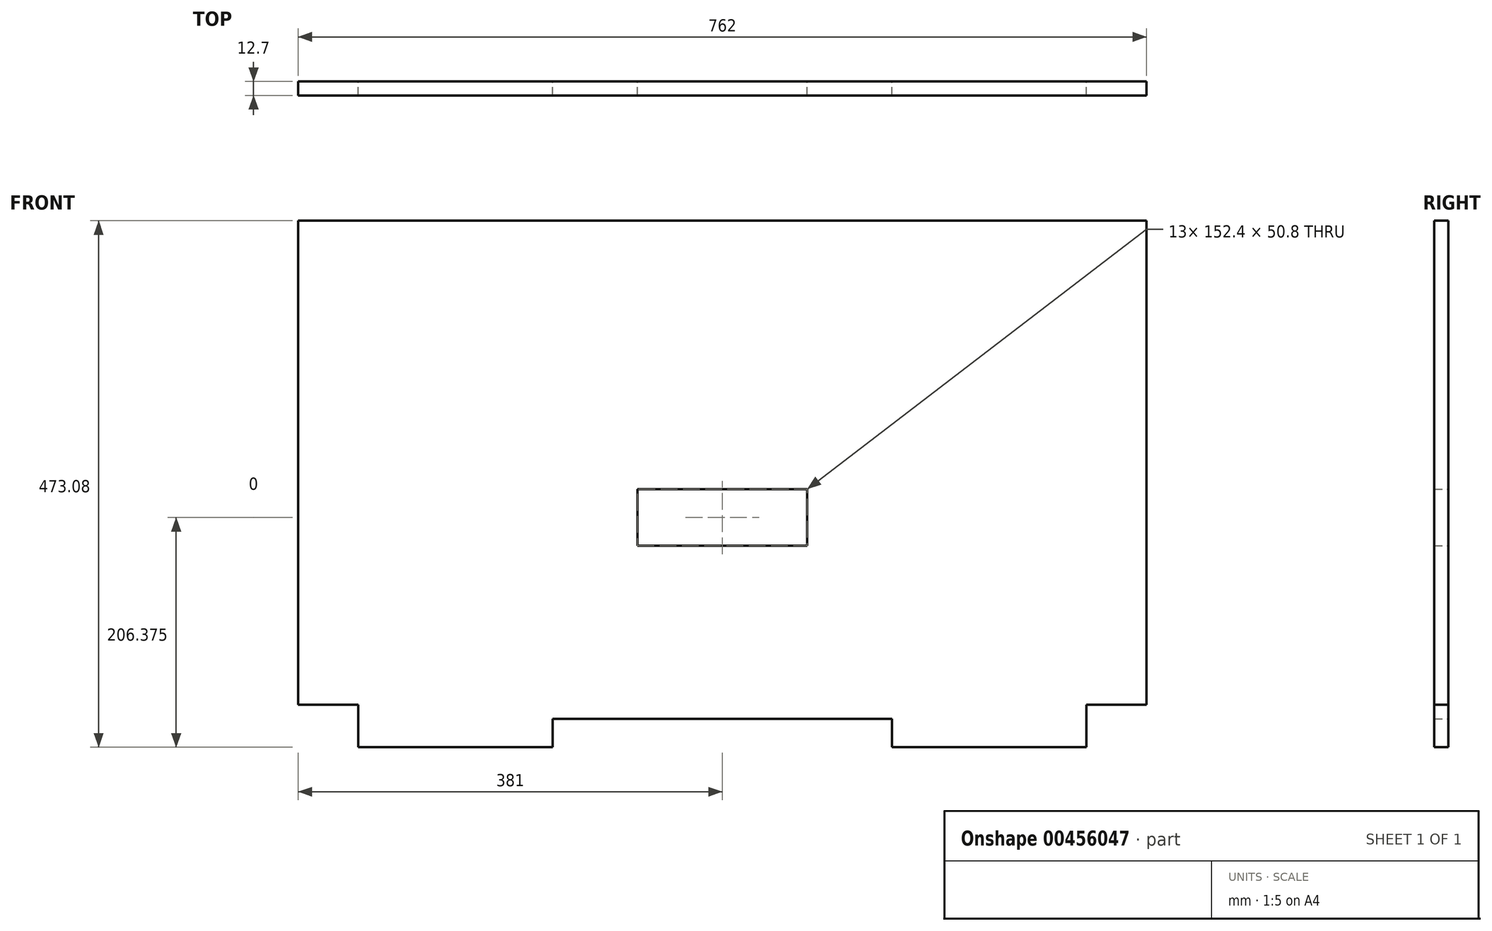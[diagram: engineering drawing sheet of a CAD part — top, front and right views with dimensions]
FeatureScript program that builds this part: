
annotation { "Feature Type Name" : "Feature", "Feature Type Description" : "" }
export const myFeature = defineFeature(function(context is Context, id is Id, definition is map)
    precondition{}
    {
        {
            var Q0;
            Q0=qCreatedBy(makeId("Front.planeOp"),FACE);
            var sketch = newSketch(context, id + "F0", { "sketchPlane" : qUnion([Q0])});
            skLineSegment(sketch, "E0.bottom", {"start": v(0, 0) * mm, "end": v(-787.4, 0) * mm});
            skLineSegment(sketch, "E0.top", {"start": v(0, 473.07) * mm, "end": v(-787.4, 473.07) * mm});
            skLineSegment(sketch, "E0.left", {"start": v(0, 0) * mm, "end": v(0, 473.07) * mm});
            skLineSegment(sketch, "E0.right", {"start": v(-787.4, 0) * mm, "end": v(-787.4, 473.07) * mm});
            skLineSegment(sketch, "E1.bottom", {"start": v(-768.35, 0) * mm, "end": v(-719.14, 0) * mm});
            skLineSegment(sketch, "E1.top", {"start": v(-768.35, 38.1) * mm, "end": v(-719.14, 38.1) * mm});
            skLineSegment(sketch, "E1.left", {"start": v(-768.35, 0) * mm, "end": v(-768.35, 38.1) * mm});
            skLineSegment(sketch, "E1.right", {"start": v(-719.14, 0) * mm, "end": v(-719.14, 38.1) * mm});
            skLineSegment(sketch, "E2.bottom", {"start": v(-546.1, 0) * mm, "end": v(-241.3, 0) * mm});
            skLineSegment(sketch, "E2.left", {"start": v(-546.1, 0) * mm, "end": v(-546.1, 25.4) * mm});
            skLineSegment(sketch, "E2.right", {"start": v(-241.3, 0) * mm, "end": v(-241.3, 25.4) * mm});
            skLineSegment(sketch, "E3", {"start": v(-393.7, 473.07) * mm, "end": v(-393.7, 0) * mm, "construction": true});
            skLineSegment(sketch, "E4.MirrorCS", {"start": v(-19.05, 0) * mm, "end": v(-68.26, 0) * mm});
            skLineSegment(sketch, "E5.MirrorCS", {"start": v(-68.26, 0) * mm, "end": v(-68.26, 38.1) * mm});
            skLineSegment(sketch, "E6.MirrorCS", {"start": v(-19.05, 0) * mm, "end": v(-19.05, 38.1) * mm});
            skLineSegment(sketch, "E7.MirrorCS", {"start": v(-19.05, 38.1) * mm, "end": v(-68.26, 38.1) * mm});
            skLineSegment(sketch, "E8", {"start": v(-546.1, 25.4) * mm, "end": v(-393.7, 25.4) * mm});
            skLineSegment(sketch, "E9", {"start": v(-393.7, 25.4) * mm, "end": v(-241.3, 25.4) * mm});
            skLineSegment(sketch, "E10", {"start": v(-768.35, 38.1) * mm, "end": v(-787.4, 38.1) * mm});
            skLineSegment(sketch, "E11.MirrorCS", {"start": v(-19.05, 38.1) * mm, "end": v(0, 38.1) * mm});
            skLineSegment(sketch, "E12.bottom", {"start": v(-393.7, 231.78) * mm, "end": v(-469.9, 231.78) * mm});
            skLineSegment(sketch, "E12.top", {"start": v(-393.7, 180.98) * mm, "end": v(-469.9, 180.98) * mm});
            skLineSegment(sketch, "E12.left", {"start": v(-393.7, 231.78) * mm, "end": v(-393.7, 180.98) * mm});
            skLineSegment(sketch, "E12.right", {"start": v(-469.9, 231.78) * mm, "end": v(-469.9, 180.98) * mm});
            skLineSegment(sketch, "E13.MirrorCS", {"start": v(-393.7, 231.78) * mm, "end": v(-317.5, 231.78) * mm});
            skLineSegment(sketch, "E14.MirrorCS", {"start": v(-317.5, 231.78) * mm, "end": v(-317.5, 180.98) * mm});
            skLineSegment(sketch, "E15.MirrorCS", {"start": v(-393.7, 180.98) * mm, "end": v(-317.5, 180.98) * mm});
            skLineSegment(sketch, "E16", {"start": v(-774.7, 473.07) * mm, "end": v(-774.7, 0) * mm});
            skLineSegment(sketch, "E17.MirrorCS", {"start": v(-12.7, 473.07) * mm, "end": v(-12.7, 0) * mm});
            skLineSegment(sketch, "E18", {"start": v(-720.72, 38.1) * mm, "end": v(-720.72, 0) * mm});
            skLineSegment(sketch, "E19.MirrorCS", {"start": v(-66.68, 38.1) * mm, "end": v(-66.68, 0) * mm});
            skSolve(sketch);
        }
        {
            var Q0;
            {var subQ15=sQuery(id+"F0.wireOp",EDGE,"E1.top");Q0=makeQuery(id+"F0.imprint","IMPRINT",FACE,{"disambiguationData":[TD([[makeQuery(id+"F0.imprint","IMPRINT",EDGE,{"derivedFrom":subQ15}),1.0]])]});}
            var Q1;
            {var subQ0=sQuery(id+"F0.wireOp",EDGE,"E5.MirrorCS");Q1=makeQuery(id+"F0.imprint","IMPRINT",FACE,{"disambiguationData":[TD([[makeQuery(id+"F0.imprint","IMPRINT",EDGE,{"derivedFrom":subQ0}),-1.0]])]});}
            var Q2;
            {var subQ0=sQuery(id+"F0.wireOp",EDGE,"E1.right");Q2=makeQuery(id+"F0.imprint","IMPRINT",FACE,{"disambiguationData":[TD([[makeQuery(id+"F0.imprint","IMPRINT",EDGE,{"derivedFrom":subQ0}),1.0]])]});}
            extrude(context, id + "F1", {"entities" : qUnion([Q0, Q1, Q2]), "depth" : 12.7 * mm});
        }
    });
